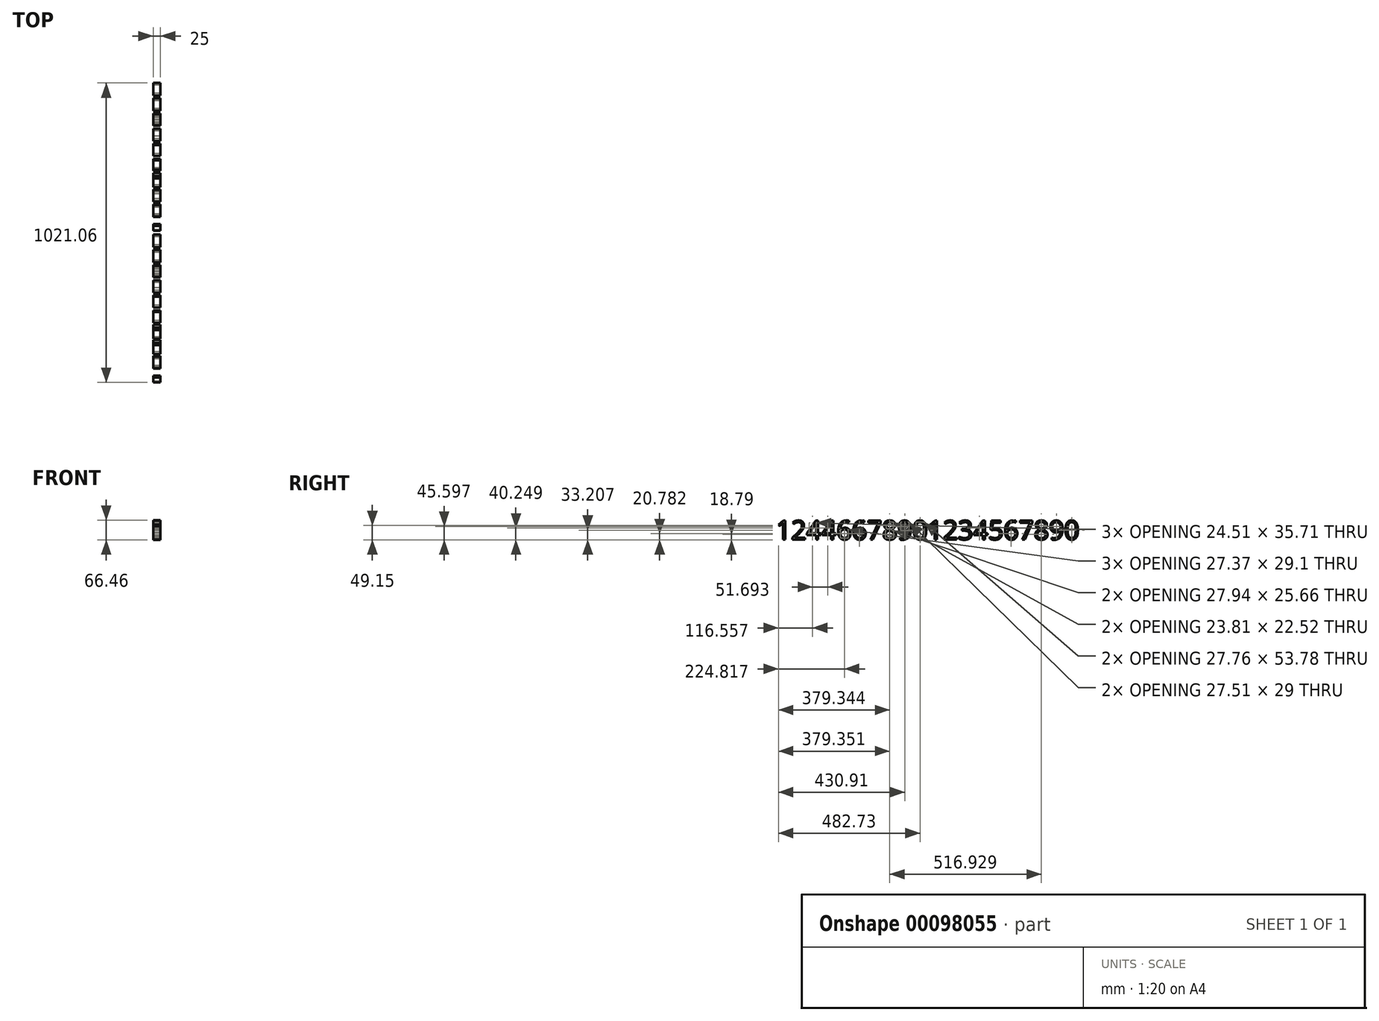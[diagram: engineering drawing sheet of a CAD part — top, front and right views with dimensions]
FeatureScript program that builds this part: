
annotation { "Feature Type Name" : "Feature", "Feature Type Description" : "" }
export const myFeature = defineFeature(function(context is Context, id is Id, definition is map)
    precondition{}
    {
        {
            var Q0;
            Q0=qCreatedBy(makeId("Right.planeOp"),FACE);
            var sketch = newSketch(context, id + "F0", { "sketchPlane" : qUnion([Q0])});
            skText(sketch, "E0", { "text": "12446678901234567890", "fontName": "OpenSans-Regular.ttf"});
            const initialGuessF0  = {"E0": [0, 0, 1, 0, 0.0651]};
            skSetInitialGuess(sketch, initialGuessF0);
            skSolve(sketch);
        }
        {
            var Q0;
            Q0 = qSketchRegion(id + "F0", true);
            extrude(context, id + "F1", {"entities" : qUnion([Q0]), "depth" : 25 * mm});
        }
    });
